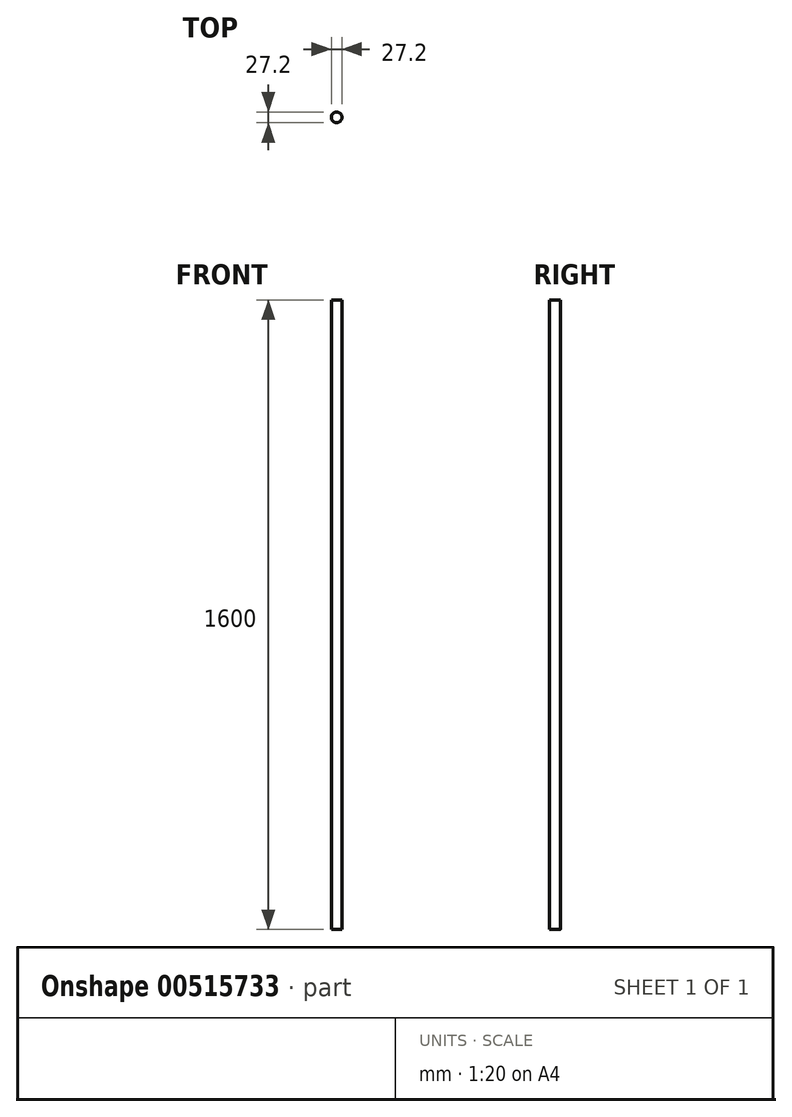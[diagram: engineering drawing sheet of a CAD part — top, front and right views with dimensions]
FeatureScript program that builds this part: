
annotation { "Feature Type Name" : "Feature", "Feature Type Description" : "" }
export const myFeature = defineFeature(function(context is Context, id is Id, definition is map)
    precondition{}
    {
        {
            var Q0;
            Q0=qCreatedBy(makeId("Top.planeOp"),FACE);
            var sketch = newSketch(context, id + "F0", { "sketchPlane" : qUnion([Q0])});
            skCircle(sketch, "E0", {"center": v(0, 0) * mm, "radius": 13.6 * mm});
            skSolve(sketch);
        }
        {
            var Q0;
            Q0 = qSketchRegion(id + "F0", true);
            extrude(context, id + "F1", {"entities" : qUnion([Q0]), "depth" : 1600 * mm, "offsetDistance" : 25 * mm});
        }
    });
